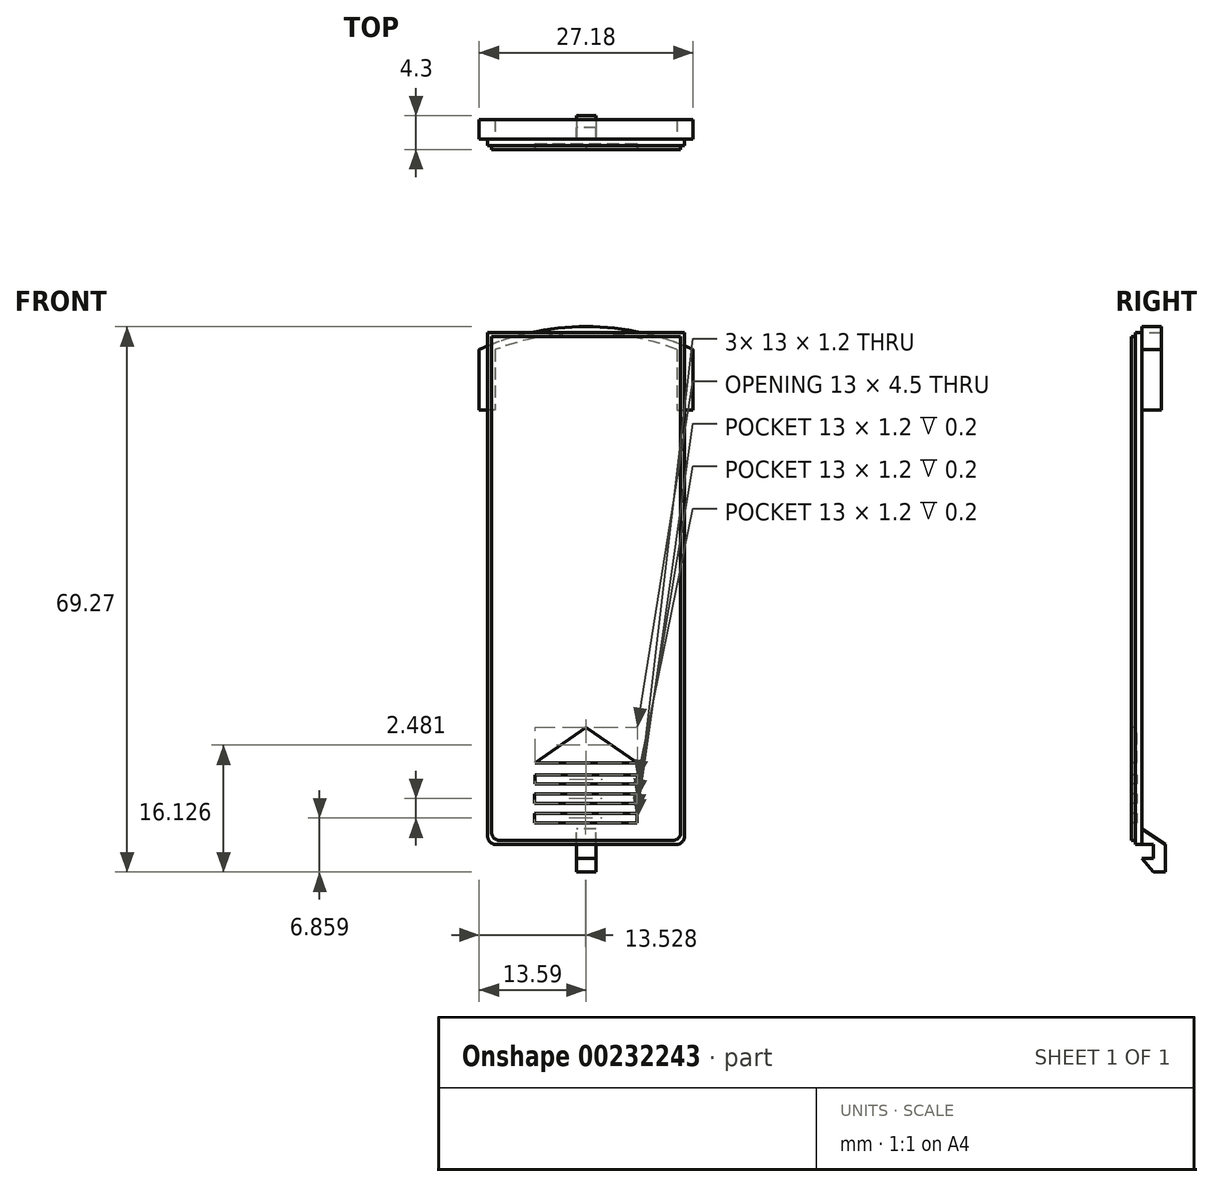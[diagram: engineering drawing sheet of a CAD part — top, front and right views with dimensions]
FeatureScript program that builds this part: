
annotation { "Feature Type Name" : "Feature", "Feature Type Description" : "" }
export const myFeature = defineFeature(function(context is Context, id is Id, definition is map)
    precondition{}
    {
        {
            var Q0;
            Q0=qCreatedBy(makeId("Front.planeOp"),FACE);
            var sketch = newSketch(context, id + "F0", { "sketchPlane" : qUnion([Q0])});
            skLineSegment(sketch, "E0.bottom", {"start": v(12.5, -32.5) * mm, "end": v(-12.5, -32.5) * mm});
            skLineSegment(sketch, "E0.top", {"start": v(12.5, 32.5) * mm, "end": v(-12.5, 32.5) * mm});
            skLineSegment(sketch, "E0.left", {"start": v(12.5, -32.5) * mm, "end": v(12.5, 32.5) * mm});
            skLineSegment(sketch, "E0.right", {"start": v(-12.5, -32.5) * mm, "end": v(-12.5, 32.5) * mm});
            skPoint(sketch, "E0.middle", {"position": v(0, 0) * mm});
            skSolve(sketch);
        }
        {
            var Q0;
            Q0=makeQuery(id+"F0.imprint","IMPRINT",FACE,{"disambiguationData":[TD([[makeQuery(id+"F0.imprint","IMPRINT",EDGE,{"derivedFrom":sQuery(id+"F0.wireOp",EDGE,"E0.bottom")}),-1.0]])]});
            extrude(context, id + "F1", {"entities" : qUnion([Q0]), "depth" : 0.8 * mm});
        }
        {
            var Q0;
            Q0=makeQuery(id+"F1.opExtrude","CAP_FACE",FACE,{"disambiguationData":[OSD([sQuery(id+"F0.wireOp",EDGE,"E0.bottom"),sQuery(id+"F0.wireOp",EDGE,"E0.top"),sQuery(id+"F0.wireOp",EDGE,"E0.left"),sQuery(id+"F0.wireOp",EDGE,"E0.right")])],"isStart":false});
            var sketch = newSketch(context, id + "F2", { "sketchPlane" : qUnion([Q0])});
            skLineSegment(sketch, "E1.bottom", {"start": v(12, -32) * mm, "end": v(-12, -32) * mm});
            skLineSegment(sketch, "E1.top", {"start": v(12, 32) * mm, "end": v(-12, 32) * mm});
            skLineSegment(sketch, "E1.left", {"start": v(12, -32) * mm, "end": v(12, 32) * mm});
            skLineSegment(sketch, "E1.right", {"start": v(-12, -32) * mm, "end": v(-12, 32) * mm});
            skPoint(sketch, "E1.middle", {"position": v(0, 0) * mm});
            skSolve(sketch);
        }
        {
            var Q0;
            Q0=makeQuery(id+"F2.imprint","IMPRINT",FACE,{"disambiguationData":[TD([[makeQuery(id+"F2.imprint","IMPRINT",EDGE,{"derivedFrom":sQuery(id+"F2.wireOp",EDGE,"E1.bottom")}),-1.0]])]});
            extrude(context, id + "F3", {"entities" : qUnion([Q0]), "depth" : 0.5 * mm});
        }
        {
            var Q0;
            Q0=makeQuery(id+"F1.opExtrude","SWEPT_EDGE",EDGE,{"disambiguationData":[OSD([sQuery(id+"F0.wireOp",EDGE,"E0.bottom"),sQuery(id+"F0.wireOp",EDGE,"E0.left")])]});
            var Q1;
            Q1=makeQuery(id+"F3.opExtrude","SWEPT_EDGE",EDGE,{"disambiguationData":[OSD([sQuery(id+"F2.wireOp",EDGE,"E1.bottom"),sQuery(id+"F2.wireOp",EDGE,"E1.left")])]});
            var Q2;
            Q2=makeQuery(id+"F3.opExtrude","SWEPT_EDGE",EDGE,{"disambiguationData":[OSD([sQuery(id+"F2.wireOp",EDGE,"E1.bottom"),sQuery(id+"F2.wireOp",EDGE,"E1.right")])]});
            var Q3;
            Q3=makeQuery(id+"F1.opExtrude","SWEPT_EDGE",EDGE,{"disambiguationData":[OSD([sQuery(id+"F0.wireOp",EDGE,"E0.bottom"),sQuery(id+"F0.wireOp",EDGE,"E0.right")])]});
            fillet(context, id + "F4", {"entities" : qUnion([Q0, Q1, Q2, Q3]), "radius" : 1 * mm, "tangentPropagation" : true, "allowEdgeOverflow" : false});
        }
        {
            var Q0;
            Q0=makeQuery(id+"F3.opExtrude","CAP_FACE",FACE,{"disambiguationData":[OSD([sQuery(id+"F2.wireOp",EDGE,"E1.bottom"),sQuery(id+"F2.wireOp",EDGE,"E1.top"),sQuery(id+"F2.wireOp",EDGE,"E1.left"),sQuery(id+"F2.wireOp",EDGE,"E1.right")])],"isStart":false});
            var sketch = newSketch(context, id + "F5", { "sketchPlane" : qUnion([Q0])});
            skPoint(sketch, "E2.0", {"position": v(0, 32) * mm});
            skLineSegment(sketch, "E3", {"start": v(0, -22.12) * mm, "end": v(-6.5, -22.12) * mm});
            skLineSegment(sketch, "E4", {"start": v(-6.5, -22.12) * mm, "end": v(0, -17.62) * mm});
            skLineSegment(sketch, "E5.MirrorCS", {"start": v(6.5, -22.12) * mm, "end": v(0, -17.62) * mm});
            skLineSegment(sketch, "E6.MirrorCS", {"start": v(0, -22.12) * mm, "end": v(6.5, -22.12) * mm});
            skLineSegment(sketch, "E7.bottom", {"start": v(0, -75.86) * mm, "end": v(-6.5, -75.86) * mm});
            skLineSegment(sketch, "E7.top", {"start": v(0, -77.06) * mm, "end": v(-6.5, -77.06) * mm});
            skLineSegment(sketch, "E7.left", {"start": v(0, -75.86) * mm, "end": v(0, -77.06) * mm});
            skLineSegment(sketch, "E7.right", {"start": v(-6.5, -75.86) * mm, "end": v(-6.5, -77.06) * mm});
            skLineSegment(sketch, "E8.MirrorCS", {"start": v(0, -75.86) * mm, "end": v(6.5, -75.86) * mm});
            skLineSegment(sketch, "E9.MirrorCS", {"start": v(0, -77.06) * mm, "end": v(6.5, -77.06) * mm});
            skLineSegment(sketch, "E10.MirrorCS", {"start": v(6.5, -75.86) * mm, "end": v(6.5, -77.06) * mm});
            skLineSegment(sketch, "E11.bottom", {"start": v(-0.06, -28.54) * mm, "end": v(-6.56, -28.54) * mm});
            skLineSegment(sketch, "E11.top", {"start": v(-0.06, -29.74) * mm, "end": v(-6.56, -29.74) * mm});
            skLineSegment(sketch, "E11.left", {"start": v(-0.06, -28.54) * mm, "end": v(-0.06, -29.74) * mm});
            skLineSegment(sketch, "E11.right", {"start": v(-6.56, -28.54) * mm, "end": v(-6.56, -29.74) * mm});
            skLineSegment(sketch, "E12.MirrorCS", {"start": v(-0.06, -28.54) * mm, "end": v(6.44, -28.54) * mm});
            skLineSegment(sketch, "E13.MirrorCS", {"start": v(-0.06, -29.74) * mm, "end": v(6.44, -29.74) * mm});
            skLineSegment(sketch, "E14.MirrorCS", {"start": v(6.44, -28.54) * mm, "end": v(6.44, -29.74) * mm});
            skLineSegment(sketch, "E15.bottom", {"start": v(31.22, -78.27) * mm, "end": v(24.72, -78.27) * mm});
            skLineSegment(sketch, "E15.top", {"start": v(31.22, -79.47) * mm, "end": v(24.72, -79.47) * mm});
            skLineSegment(sketch, "E15.left", {"start": v(31.22, -78.27) * mm, "end": v(31.22, -79.47) * mm});
            skLineSegment(sketch, "E15.right", {"start": v(24.72, -78.27) * mm, "end": v(24.72, -79.47) * mm});
            skLineSegment(sketch, "E16.MirrorCS", {"start": v(31.22, -78.27) * mm, "end": v(37.72, -78.27) * mm});
            skLineSegment(sketch, "E17.MirrorCS", {"start": v(31.22, -79.47) * mm, "end": v(37.72, -79.47) * mm});
            skLineSegment(sketch, "E18.MirrorCS", {"start": v(37.72, -78.27) * mm, "end": v(37.72, -79.47) * mm});
            skLineSegment(sketch, "E19.bottom", {"start": v(0, -23.64) * mm, "end": v(-6.5, -23.64) * mm});
            skLineSegment(sketch, "E19.top", {"start": v(0, -24.84) * mm, "end": v(-6.5, -24.84) * mm});
            skLineSegment(sketch, "E19.left", {"start": v(0, -23.64) * mm, "end": v(0, -24.84) * mm});
            skLineSegment(sketch, "E19.right", {"start": v(-6.5, -23.64) * mm, "end": v(-6.5, -24.84) * mm});
            skLineSegment(sketch, "E20.MirrorCS", {"start": v(0, -23.64) * mm, "end": v(6.5, -23.64) * mm});
            skLineSegment(sketch, "E21.MirrorCS", {"start": v(0, -24.84) * mm, "end": v(6.5, -24.84) * mm});
            skLineSegment(sketch, "E22.MirrorCS", {"start": v(6.5, -23.64) * mm, "end": v(6.5, -24.84) * mm});
            skLineSegment(sketch, "E23.bottom", {"start": v(-0.06, -26.06) * mm, "end": v(-6.56, -26.06) * mm});
            skLineSegment(sketch, "E23.top", {"start": v(-0.06, -27.26) * mm, "end": v(-6.56, -27.26) * mm});
            skLineSegment(sketch, "E23.left", {"start": v(-0.06, -26.06) * mm, "end": v(-0.06, -27.26) * mm});
            skLineSegment(sketch, "E23.right", {"start": v(-6.56, -26.06) * mm, "end": v(-6.56, -27.26) * mm});
            skLineSegment(sketch, "E24.MirrorCS", {"start": v(-0.06, -26.06) * mm, "end": v(6.44, -26.06) * mm});
            skLineSegment(sketch, "E25.MirrorCS", {"start": v(-0.06, -27.26) * mm, "end": v(6.44, -27.26) * mm});
            skLineSegment(sketch, "E26.MirrorCS", {"start": v(6.44, -26.06) * mm, "end": v(6.44, -27.26) * mm});
            skSolve(sketch);
        }
        {
            var Q0;
            Q0=makeQuery(id+"F5.imprint","IMPRINT",FACE,{"disambiguationData":[TD([[makeQuery(id+"F5.imprint","IMPRINT",EDGE,{"derivedFrom":sQuery(id+"F5.wireOp",EDGE,"E3")}),-1.0]])]});
            var Q1;
            Q1=makeQuery(id+"F5.imprint","IMPRINT",FACE,{"disambiguationData":[TD([[makeQuery(id+"F5.imprint","IMPRINT",EDGE,{"derivedFrom":sQuery(id+"F5.wireOp",EDGE,"E19.bottom")}),1.0]])]});
            var Q2;
            Q2=makeQuery(id+"F5.imprint","IMPRINT",FACE,{"disambiguationData":[TD([[makeQuery(id+"F5.imprint","IMPRINT",EDGE,{"derivedFrom":sQuery(id+"F5.wireOp",EDGE,"E19.left")}),1.0]])]});
            var Q3;
            Q3=makeQuery(id+"F5.imprint","IMPRINT",FACE,{"disambiguationData":[TD([[makeQuery(id+"F5.imprint","IMPRINT",EDGE,{"derivedFrom":sQuery(id+"F5.wireOp",EDGE,"E23.left")}),1.0]])]});
            var Q4;
            Q4=makeQuery(id+"F5.imprint","IMPRINT",FACE,{"disambiguationData":[TD([[makeQuery(id+"F5.imprint","IMPRINT",EDGE,{"derivedFrom":sQuery(id+"F5.wireOp",EDGE,"E23.bottom")}),1.0]])]});
            var Q5;
            Q5=makeQuery(id+"F5.imprint","IMPRINT",FACE,{"disambiguationData":[TD([[makeQuery(id+"F5.imprint","IMPRINT",EDGE,{"derivedFrom":sQuery(id+"F5.wireOp",EDGE,"E11.bottom")}),1.0]])]});
            var Q6;
            Q6=makeQuery(id+"F5.imprint","IMPRINT",FACE,{"disambiguationData":[TD([[makeQuery(id+"F5.imprint","IMPRINT",EDGE,{"derivedFrom":sQuery(id+"F5.wireOp",EDGE,"E11.left")}),1.0]])]});
            extrude(context, id + "F6", {"entities" : qUnion([Q0, Q1, Q2, Q3, Q4, Q5, Q6]), "operationType" : NewBodyOperationType.REMOVE, "oppositeDirection" : true, "depth" : 0.7 * mm});
        }
        {
            var Q0;
            Q0=qCreatedBy(makeId("Right.planeOp"),FACE);
            var sketch = newSketch(context, id + "F7", { "sketchPlane" : qUnion([Q0])});
            skLineSegment(sketch, "E27", {"start": v(0, -32.5) * mm, "end": v(0, -30.5) * mm});
            skLineSegment(sketch, "E28", {"start": v(0, -30.5) * mm, "end": v(3, -32.5) * mm});
            skLineSegment(sketch, "E29", {"start": v(3, -32.5) * mm, "end": v(0, -32.5) * mm});
            skPoint(sketch, "E30.3", {"position": v(0, -32.5) * mm});
            skSolve(sketch);
        }
        {
            var Q0;
            Q0=makeQuery(id+"F7.imprint","IMPRINT",FACE,{"disambiguationData":[TD([[makeQuery(id+"F7.imprint","IMPRINT",EDGE,{"derivedFrom":sQuery(id+"F7.wireOp",EDGE,"E27")}),-1.0]])]});
            extrude(context, id + "F8", {"entities" : qUnion([Q0]), "operationType" : NewBodyOperationType.ADD, "endBound" : BoundingType.SYMMETRIC, "depth" : 2.5 * mm});
        }
        {
            var Q0;
            Q0=makeQuery(id+"F8.boolean.opBoolean","MERGE",FACE,{"derivedFrom":[makeQuery(id+"F1.opExtrude","SWEPT_FACE",FACE,{"disambiguationData":[OSD([sQuery(id+"F0.wireOp",EDGE,"E0.bottom")])]}),makeQuery(id+"F8.opExtrude","SWEPT_FACE",FACE,{"disambiguationData":[OSD([sQuery(id+"F7.wireOp",EDGE,"E29")])]})]});
            var sketch = newSketch(context, id + "F9", { "sketchPlane" : qUnion([Q0])});
            skLineSegment(sketch, "E31.bottom", {"start": v(1.25, -3) * mm, "end": v(-1.25, -3) * mm});
            skLineSegment(sketch, "E31.top", {"start": v(1.25, -1.5) * mm, "end": v(-1.25, -1.5) * mm});
            skLineSegment(sketch, "E31.left", {"start": v(1.25, -3) * mm, "end": v(1.25, -1.5) * mm});
            skLineSegment(sketch, "E31.right", {"start": v(-1.25, -3) * mm, "end": v(-1.25, -1.5) * mm});
            skSolve(sketch);
        }
        {
            var Q0;
            Q0=makeQuery(id+"F9.imprint","IMPRINT",FACE,{"disambiguationData":[TD([[makeQuery(id+"F9.imprint","IMPRINT",EDGE,{"derivedFrom":sQuery(id+"F9.wireOp",EDGE,"E31.bottom")}),-1.0]])]});
            extrude(context, id + "F10", {"entities" : qUnion([Q0]), "operationType" : NewBodyOperationType.ADD, "depth" : 3.5 * mm});
        }
        {
            var Q0;
            Q0=qCreatedBy(makeId("Right.planeOp"),FACE);
            var sketch = newSketch(context, id + "F11", { "sketchPlane" : qUnion([Q0])});
            skLineSegment(sketch, "E32", {"start": v(1.5, -34.25) * mm, "end": v(0, -34.25) * mm});
            skLineSegment(sketch, "E33", {"start": v(0, -34.25) * mm, "end": v(1.5, -36) * mm});
            skLineSegment(sketch, "E34", {"start": v(1.5, -34.25) * mm, "end": v(1.5, -36) * mm});
            skSolve(sketch);
        }
        {
            var Q0;
            Q0=makeQuery(id+"F11.imprint","IMPRINT",FACE,{"disambiguationData":[TD([[makeQuery(id+"F11.imprint","IMPRINT",EDGE,{"derivedFrom":sQuery(id+"F11.wireOp",EDGE,"E32")}),1.0]])]});
            extrude(context, id + "F12", {"entities" : qUnion([Q0]), "operationType" : NewBodyOperationType.ADD, "endBound" : BoundingType.SYMMETRIC, "depth" : 2.5 * mm});
        }
        {
            var Q0;
            Q0=qCreatedBy(makeId("Front.planeOp"),FACE);
            var sketch = newSketch(context, id + "F13", { "sketchPlane" : qUnion([Q0])});
            skArc(sketch, "E35", {"start": v(0, 32.5) * mm, "mid": v(-5.88, 31.96) * mm, "end": v(-11.56, 30.37) * mm});
            skLineSegment(sketch, "E36", {"start": v(-11.56, 30.37) * mm, "end": v(-11.56, 22.67) * mm});
            skLineSegment(sketch, "E37", {"start": v(-11.56, 22.67) * mm, "end": v(-13.6, 22.67) * mm});
            skLineSegment(sketch, "E38", {"start": v(-13.6, 22.67) * mm, "end": v(-13.6, 30.37) * mm});
            skArc(sketch, "E39", {"start": v(0, 33.27) * mm, "mid": v(-6.95, 32.54) * mm, "end": v(-13.6, 30.37) * mm});
            skArc(sketch, "E40.MirrorCS", {"start": v(0, 33.27) * mm, "mid": v(6.95, 32.54) * mm, "end": v(13.6, 30.37) * mm});
            skLineSegment(sketch, "E41.MirrorCS", {"start": v(13.6, 22.67) * mm, "end": v(13.6, 30.37) * mm});
            skLineSegment(sketch, "E42.MirrorCS", {"start": v(11.56, 22.67) * mm, "end": v(13.6, 22.67) * mm});
            skLineSegment(sketch, "E43.MirrorCS", {"start": v(11.56, 30.37) * mm, "end": v(11.56, 22.67) * mm});
            skArc(sketch, "E44.MirrorCS", {"start": v(0, 32.5) * mm, "mid": v(5.88, 31.96) * mm, "end": v(11.56, 30.37) * mm});
            skSolve(sketch);
        }
        {
            var Q0;
            Q0=makeQuery(id+"F13.imprint","IMPRINT",FACE,{"disambiguationData":[TD([[makeQuery(id+"F13.imprint","IMPRINT",EDGE,{"derivedFrom":sQuery(id+"F13.wireOp",EDGE,"E35")}),-1.0]])]});
            extrude(context, id + "F14", {"entities" : qUnion([Q0]), "oppositeDirection" : true, "depth" : 2.5 * mm});
        }
    });
